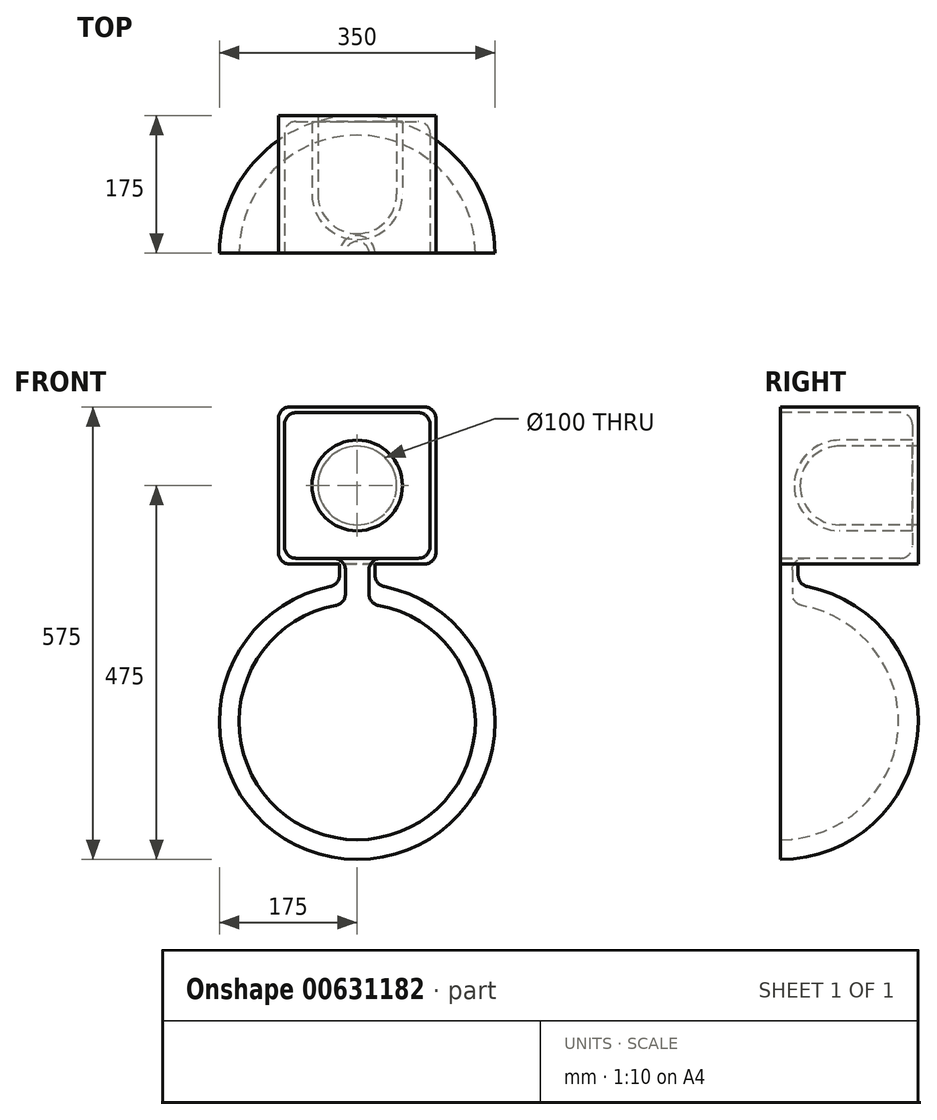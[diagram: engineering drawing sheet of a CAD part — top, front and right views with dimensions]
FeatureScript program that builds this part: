
annotation { "Feature Type Name" : "Feature", "Feature Type Description" : "" }
export const myFeature = defineFeature(function(context is Context, id is Id, definition is map)
    precondition{}
    {
        {
            var Q0;
            Q0=qCreatedBy(makeId("Front.planeOp"),FACE);
            var sketch = newSketch(context, id + "F0", { "sketchPlane" : qUnion([Q0])});
            skLineSegment(sketch, "E0.bottom", {"start": v(-100, 100) * mm, "end": v(100, 100) * mm});
            skLineSegment(sketch, "E0.top", {"start": v(-100, -100) * mm, "end": v(100, -100) * mm});
            skLineSegment(sketch, "E0.left", {"start": v(-100, 100) * mm, "end": v(-100, -100) * mm});
            skLineSegment(sketch, "E0.right", {"start": v(100, 100) * mm, "end": v(100, -100) * mm});
            skPoint(sketch, "E1", {"position": v(0, 100) * mm});
            skPoint(sketch, "E2", {"position": v(100, 0) * mm});
            skSolve(sketch);
        }
        {
            var Q0;
            Q0=makeQuery(id+"F0.imprint","IMPRINT",FACE,{"disambiguationData":[TD([[makeQuery(id+"F0.imprint","IMPRINT",EDGE,{"derivedFrom":sQuery(id+"F0.wireOp",EDGE,"E0.bottom")}),-1.0]])]});
            extrude(context, id + "F1", {"entities" : qUnion([Q0]), "oppositeDirection" : true, "depth" : 175 * mm, "offsetDistance" : 25 * mm});
        }
        {
            var Q0;
            Q0=qCreatedBy(makeId("Right.planeOp"),FACE);
            var sketch = newSketch(context, id + "F2", { "sketchPlane" : qUnion([Q0])});
            skPoint(sketch, "E3", {"position": v(175, 0) * mm});
            skLineSegment(sketch, "E4", {"start": v(225, 0) * mm, "end": v(125, 0) * mm});
            skLineSegment(sketch, "E5", {"start": v(125, 0) * mm, "end": v(25, 0) * mm});
            skPoint(sketch, "E6", {"position": v(75, 0) * mm});
            skCircle(sketch, "E7", {"center": v(75, 0) * mm, "radius": 50 * mm});
            skPoint(sketch, "E8", {"position": v(75, 50) * mm});
            skPoint(sketch, "E9", {"position": v(75, -50) * mm});
            skLineSegment(sketch, "E10", {"start": v(75, -50) * mm, "end": v(190.75, -50) * mm});
            skLineSegment(sketch, "E11", {"start": v(190.75, -50) * mm, "end": v(190.75, 50) * mm});
            skLineSegment(sketch, "E12", {"start": v(190.75, 50) * mm, "end": v(75, 50) * mm});
            skSolve(sketch);
        }
        {
            var Q0;
            {var subQ5=sQuery(id+"F2.wireOp",EDGE,"E12");Q0=makeQuery(id+"F2.imprint","IMPRINT",FACE,{"disambiguationData":[TD([[makeQuery(id+"F2.imprint","IMPRINT",EDGE,{"derivedFrom":subQ5}),1.0]])]});}
            var Q1;
            {var subQ0=sQuery(id+"F2.wireOp",EDGE,"E5");Q1=makeQuery(id+"F2.imprint","IMPRINT",FACE,{"disambiguationData":[TD([[makeQuery(id+"F2.imprint","IMPRINT",EDGE,{"derivedFrom":subQ0}),-1.0]])]});}
            var Q2;
            Q2=sQuery(id+"F2.wireOp",EDGE,"E5");
            revolve(context, id + "F3", {"operationType" : NewBodyOperationType.REMOVE, "surfaceOperationType" : NewSurfaceOperationType.NEW, "entities" : qUnion([Q0, Q1]), "axis" : qUnion([Q2]), "revolveType" : RevolveType.FULL, "oppositeDirection" : true});
        }
        {
            var Q0;
            Q0=makeQuery(id+"F1.opExtrude","CAP_FACE",FACE,{"disambiguationData":[OSD([sQuery(id+"F0.wireOp",EDGE,"E0.bottom"),sQuery(id+"F0.wireOp",EDGE,"E0.top"),sQuery(id+"F0.wireOp",EDGE,"E0.left"),sQuery(id+"F0.wireOp",EDGE,"E0.right")])],"isStart":true});
            shell(context, id + "F4", {"entities" : qUnion([Q0]), "thickness" : 7.5 * mm});
        }
        {
            var Q0;
            Q0=qCreatedBy(makeId("Top.planeOp"),FACE);
            cPlane(context, id + "F5", {"entities" : qUnion([Q0]), "cplaneType" : CPlaneType.OFFSET, "offset" : 100 * mm, "oppositeDirection" : true, "width" : 150 * mm, "height" : 150 * mm});
        }
        {
            var Q0;
            Q0=qCreatedBy(id+"F5.planeOp",FACE);
            var sketch = newSketch(context, id + "F6", { "sketchPlane" : qUnion([Q0])});
            skCircle(sketch, "E13", {"center": v(0, 0) * mm, "radius": 22.5 * mm});
            skCircle(sketch, "E14", {"center": v(0, 0) * mm, "radius": 15 * mm});
            skPoint(sketch, "E15", {"position": v(-15, 0) * mm});
            skLineSegment(sketch, "E16", {"start": v(-15, 0) * mm, "end": v(-22.5, 0) * mm});
            skLineSegment(sketch, "E17", {"start": v(15, 0) * mm, "end": v(22.5, 0) * mm});
            skSolve(sketch);
        }
        {
            var Q0;
            {var subQ0=sQuery(id+"F6.wireOp",EDGE,"E14");var subQ1=makeQuery(id+"F6.imprint","INTERSECT",VERTEX,{"derivedFrom":[subQ0,sQuery(id+"F6.wireOp",EDGE,"E16")]});Q0=makeQuery(id+"F6.imprint","IMPRINT",FACE,{"disambiguationData":[TD([[makeQuery(id+"F6.imprint","IMPRINT",EDGE,{"disambiguationData":[TD([[subQ1,1.0]])],"derivedFrom":subQ0}),1.0]])]});}
            extrude(context, id + "F7", {"entities" : qUnion([Q0]), "operationType" : NewBodyOperationType.REMOVE, "depth" : 25 * mm, "offsetDistance" : 25 * mm});
        }
        {
            var Q0;
            {var subQ0=sQuery(id+"F6.wireOp",EDGE,"E16");Q0=makeQuery(id+"F6.imprint","IMPRINT",FACE,{"disambiguationData":[TD([[makeQuery(id+"F6.imprint","IMPRINT",EDGE,{"derivedFrom":subQ0}),-1.0]])]});}
            extrude(context, id + "F8", {"entities" : qUnion([Q0]), "operationType" : NewBodyOperationType.ADD, "oppositeDirection" : true, "depth" : 50 * mm, "offsetDistance" : 25 * mm});
        }
        {
            var Q0;
            Q0=qCreatedBy(makeId("Right.planeOp"),FACE);
            var sketch = newSketch(context, id + "F9", { "sketchPlane" : qUnion([Q0])});
            skPoint(sketch, "E18", {"position": v(0, -300) * mm});
            skCircle(sketch, "E19", {"center": v(0, -300) * mm, "radius": 150 * mm});
            skPoint(sketch, "E20", {"position": v(0, -150) * mm});
            skPoint(sketch, "E21", {"position": v(0, -125) * mm});
            skCircle(sketch, "E22", {"center": v(0, -300) * mm, "radius": 175 * mm});
            skLineSegment(sketch, "E23", {"start": v(0, -125) * mm, "end": v(0, -150) * mm});
            skLineSegment(sketch, "E24", {"start": v(0, -450) * mm, "end": v(0, -475) * mm});
            skSolve(sketch);
        }
        {
            var Q0;
            {var subQ0=sQuery(id+"F9.wireOp",EDGE,"E23");Q0=makeQuery(id+"F9.imprint","IMPRINT",FACE,{"disambiguationData":[TD([[makeQuery(id+"F9.imprint","IMPRINT",EDGE,{"derivedFrom":subQ0}),1.0]])]});}
            var Q1;
            Q1=sQuery(id+"F9.wireOp",EDGE,"E23");
            revolve(context, id + "F10", {"operationType" : NewBodyOperationType.ADD, "surfaceOperationType" : NewSurfaceOperationType.NEW, "entities" : qUnion([Q0]), "axis" : qUnion([Q1]), "revolveType" : RevolveType.TWO_DIRECTIONS, "angle" : 90 * degree, "angleBack" : 270 * degree});
        }
        {
            var Q0;
            {var subQ0=sQuery(id+"F6.wireOp",EDGE,"E14");var subQ1=makeQuery(id+"F6.imprint","INTERSECT",VERTEX,{"derivedFrom":[subQ0,sQuery(id+"F6.wireOp",EDGE,"E16")]});Q0=makeQuery(id+"F6.imprint","IMPRINT",FACE,{"disambiguationData":[TD([[makeQuery(id+"F6.imprint","IMPRINT",EDGE,{"disambiguationData":[TD([[subQ1,1.0]])],"derivedFrom":subQ0}),1.0]])]});}
            extrude(context, id + "F11", {"entities" : qUnion([Q0]), "operationType" : NewBodyOperationType.REMOVE, "oppositeDirection" : true, "depth" : 100 * mm, "offsetDistance" : 25 * mm});
        }
        {
            var Q0;
            Q0=makeQuery(id+"F4.opShell","OFFSET_EDGE",EDGE,{"disambiguationData":[OSD([sQuery(id+"F0.wireOp",EDGE,"E0.top"),sQuery(id+"F0.wireOp",EDGE,"E0.left")])]});
            var Q1;
            {var subQ0=sQuery(id+"F0.wireOp",EDGE,"E0.left");Q1=makeQuery(id+"F4.opShell","OFFSET_EDGE",EDGE,{"disambiguationData":[OSD([subQ0]),TDD([makeQuery(id+"F1.opExtrude","CAP_EDGE",EDGE,{"disambiguationData":[OSD([subQ0])],"isStart":false})])]});}
            var Q2;
            {var subQ0=sQuery(id+"F0.wireOp",EDGE,"E0.top");Q2=makeQuery(id+"F4.opShell","OFFSET_EDGE",EDGE,{"disambiguationData":[OSD([subQ0]),TDD([makeQuery(id+"F1.opExtrude","CAP_EDGE",EDGE,{"disambiguationData":[OSD([subQ0])],"isStart":false})])]});}
            var Q3;
            {var subQ0=sQuery(id+"F0.wireOp",EDGE,"E0.right");Q3=makeQuery(id+"F4.opShell","OFFSET_EDGE",EDGE,{"disambiguationData":[OSD([subQ0]),TDD([makeQuery(id+"F1.opExtrude","CAP_EDGE",EDGE,{"disambiguationData":[OSD([subQ0])],"isStart":false})])]});}
            var Q4;
            Q4=makeQuery(id+"F4.opShell","OFFSET_EDGE",EDGE,{"disambiguationData":[OSD([sQuery(id+"F0.wireOp",EDGE,"E0.top"),sQuery(id+"F0.wireOp",EDGE,"E0.right")])]});
            var Q5;
            Q5=makeQuery(id+"F4.opShell","OFFSET_EDGE",EDGE,{"disambiguationData":[OSD([sQuery(id+"F0.wireOp",EDGE,"E0.bottom"),sQuery(id+"F0.wireOp",EDGE,"E0.right")])]});
            var Q6;
            {var subQ0=sQuery(id+"F0.wireOp",EDGE,"E0.bottom");Q6=makeQuery(id+"F4.opShell","OFFSET_EDGE",EDGE,{"disambiguationData":[OSD([subQ0]),TDD([makeQuery(id+"F1.opExtrude","CAP_EDGE",EDGE,{"disambiguationData":[OSD([subQ0])],"isStart":false})])]});}
            var Q7;
            Q7=makeQuery(id+"F4.opShell","OFFSET_EDGE",EDGE,{"disambiguationData":[OSD([sQuery(id+"F0.wireOp",EDGE,"E0.bottom"),sQuery(id+"F0.wireOp",EDGE,"E0.left")])]});
            var Q8;
            Q8=makeQuery(id+"F1.opExtrude","SWEPT_EDGE",EDGE,{"disambiguationData":[OSD([sQuery(id+"F0.wireOp",EDGE,"E0.bottom"),sQuery(id+"F0.wireOp",EDGE,"E0.left")])]});
            var Q9;
            Q9=makeQuery(id+"F1.opExtrude","SWEPT_EDGE",EDGE,{"disambiguationData":[OSD([sQuery(id+"F0.wireOp",EDGE,"E0.bottom"),sQuery(id+"F0.wireOp",EDGE,"E0.right")])]});
            var Q10;
            Q10=makeQuery(id+"F1.opExtrude","SWEPT_EDGE",EDGE,{"disambiguationData":[OSD([sQuery(id+"F0.wireOp",EDGE,"E0.top"),sQuery(id+"F0.wireOp",EDGE,"E0.right")])]});
            var Q11;
            Q11=makeQuery(id+"F1.opExtrude","SWEPT_EDGE",EDGE,{"disambiguationData":[OSD([sQuery(id+"F0.wireOp",EDGE,"E0.top"),sQuery(id+"F0.wireOp",EDGE,"E0.left")])]});
            var Q12;
            Q12=makeQuery(id+"F7.boolean.opBoolean","INTERSECT",EDGE,{"derivedFrom":[makeQuery(id+"F4.opShell","OFFSET_FACE",FACE,{"disambiguationData":[OSD([sQuery(id+"F0.wireOp",EDGE,"E0.top")])]}),makeQuery(id+"F7.opExtrude","SWEPT_FACE",FACE,{"disambiguationData":[OSD([sQuery(id+"F6.wireOp",EDGE,"E14")])]})]});
            var Q13;
            Q13=makeQuery(id+"F8.opExtrude","CAP_EDGE",EDGE,{"disambiguationData":[OSD([sQuery(id+"F6.wireOp",EDGE,"E13")])],"isStart":true});
            var Q14;
            Q14=makeQuery(id+"F10.boolean.opBoolean","INTERSECT",EDGE,{"derivedFrom":[makeQuery(id+"F8.opExtrude","SWEPT_FACE",FACE,{"disambiguationData":[OSD([sQuery(id+"F6.wireOp",EDGE,"E13")])]}),makeQuery(id+"F10.opRevolve","SWEPT_FACE",FACE,{"disambiguationData":[OSD([sQuery(id+"F9.wireOp",EDGE,"E22")])]})]});
            var Q15;
            Q15=makeQuery(id+"F11.boolean.opBoolean","INTERSECT",EDGE,{"derivedFrom":[makeQuery(id+"F10.opRevolve","SWEPT_FACE",FACE,{"disambiguationData":[OSD([sQuery(id+"F9.wireOp",EDGE,"E19")])]}),makeQuery(id+"F11.opExtrude","SWEPT_FACE",FACE,{"disambiguationData":[OSD([sQuery(id+"F6.wireOp",EDGE,"E14")])]})]});
            fillet(context, id + "F12", {"entities" : qUnion([Q0, Q1, Q2, Q3, Q4, Q5, Q6, Q7, Q8, Q9, Q10, Q11, Q12, Q13, Q14, Q15]), "radius" : 15 * mm, "tangentPropagation" : true, "allowEdgeOverflow" : false});
        }
        {
            var Q0;
            Q0=qCreatedBy(makeId("Front.planeOp"),FACE);
            cPlane(context, id + "F13", {"entities" : qUnion([Q0]), "cplaneType" : CPlaneType.OFFSET, "offset" : 175 * mm, "oppositeDirection" : true, "width" : 150 * mm, "height" : 150 * mm});
        }
    });
